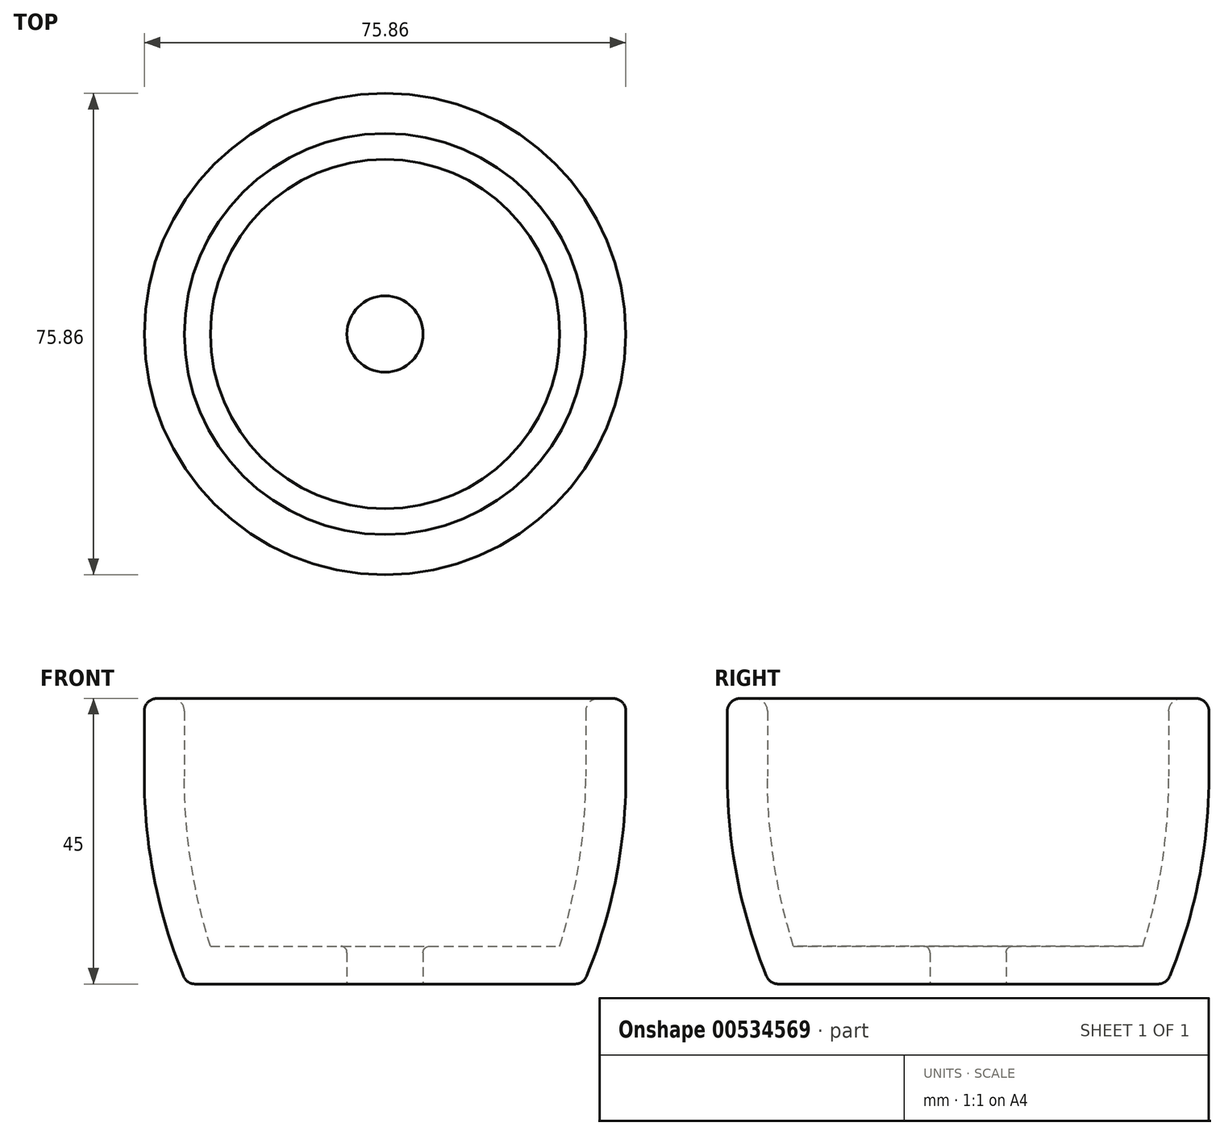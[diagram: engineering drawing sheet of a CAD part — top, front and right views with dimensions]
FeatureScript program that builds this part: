
annotation { "Feature Type Name" : "Feature", "Feature Type Description" : "" }
export const myFeature = defineFeature(function(context is Context, id is Id, definition is map)
    precondition{}
    {
        {
            var Q0;
            Q0=qCreatedBy(makeId("Front.planeOp"),FACE);
            var sketch = newSketch(context, id + "F0", { "sketchPlane" : qUnion([Q0])});
            skLineSegment(sketch, "E0", {"start": v(-37.93, 45) * mm, "end": v(-37.93, 32.73) * mm});
            skArc(sketch, "E1", {"start": v(-37.93, 32.73) * mm, "mid": v(-36.24, 16.03) * mm, "end": v(-31.24, 0) * mm});
            skLineSegment(sketch, "E2", {"start": v(-31.24, 0) * mm, "end": v(0, 0) * mm});
            skLineSegment(sketch, "E3", {"start": v(0, 0) * mm, "end": v(0, 5.95) * mm});
            skLineSegment(sketch, "E4", {"start": v(0, 5.95) * mm, "end": v(-27.52, 5.95) * mm});
            skLineSegment(sketch, "E5", {"start": v(-37.93, 45) * mm, "end": v(-31.61, 45) * mm});
            skLineSegment(sketch, "E6", {"start": v(-31.61, 45) * mm, "end": v(-31.61, 32.73) * mm});
            skArc(sketch, "E7", {"start": v(-31.61, 32.73) * mm, "mid": v(-30.58, 19.18) * mm, "end": v(-27.52, 5.95) * mm});
            skSolve(sketch);
        }
        {
            var Q0;
            Q0=makeQuery(id+"F0.imprint","IMPRINT",FACE,{"disambiguationData":[TD([[makeQuery(id+"F0.imprint","IMPRINT",EDGE,{"derivedFrom":sQuery(id+"F0.wireOp",EDGE,"E0")}),1.0]])]});
            var Q1;
            Q1=sQuery(id+"F0.wireOp",EDGE,"E3");
            revolve(context, id + "F1", {"entities" : qUnion([Q0]), "axis" : qUnion([Q1]), "revolveType" : RevolveType.FULL});
        }
        {
            var Q0;
            Q0=makeQuery(id+"F1.opRevolve","SWEPT_EDGE",EDGE,{"disambiguationData":[OSD([sQuery(id+"F0.wireOp",EDGE,"E5"),sQuery(id+"F0.wireOp",EDGE,"E6")])]});
            fillet(context, id + "F2", {"entities" : qUnion([Q0]), "radius" : 2 * mm, "tangentPropagation" : true, "allowEdgeOverflow" : false});
        }
        {
            var Q0;
            Q0=makeQuery(id+"F1.opRevolve","SWEPT_EDGE",EDGE,{"disambiguationData":[OSD([sQuery(id+"F0.wireOp",EDGE,"E0"),sQuery(id+"F0.wireOp",EDGE,"E5")])]});
            var Q1;
            Q1=makeQuery(id+"F1.opRevolve","SWEPT_EDGE",EDGE,{"disambiguationData":[OSD([sQuery(id+"F0.wireOp",EDGE,"E1"),sQuery(id+"F0.wireOp",EDGE,"E2")])]});
            fillet(context, id + "F3", {"entities" : qUnion([Q0, Q1]), "radius" : 2 * mm, "tangentPropagation" : true, "allowEdgeOverflow" : false});
        }
        {
            var Q0;
            Q0=makeQuery(id+"F1.opRevolve","SWEPT_FACE",FACE,{"disambiguationData":[OSD([sQuery(id+"F0.wireOp",EDGE,"E2")])]});
            var sketch = newSketch(context, id + "F4", { "sketchPlane" : qUnion([Q0])});
            skCircle(sketch, "E8", {"center": v(0, 0) * mm, "radius": 6 * mm});
            skSolve(sketch);
        }
        {
            var Q0;
            Q0=makeQuery(id+"F4.imprint","IMPRINT",FACE,{"disambiguationData":[TD([[makeQuery(id+"F4.imprint","IMPRINT",EDGE,{"derivedFrom":sQuery(id+"F4.wireOp",EDGE,"E8")}),1.0]])]});
            extrude(context, id + "F5", {"entities" : qUnion([Q0]), "operationType" : NewBodyOperationType.REMOVE, "oppositeDirection" : true, "depth" : 25 * mm, "offsetDistance" : 25 * mm});
        }
        {
            var Q0;
            Q0=makeQuery(id+"F5.boolean.opBoolean","COPY",EDGE,{"derivedFrom":makeQuery(id+"F5.opExtrude","CAP_EDGE",EDGE,{"disambiguationData":[OSD([sQuery(id+"F4.wireOp",EDGE,"E8")])],"isStart":true})});
            var Q1;
            Q1=makeQuery(id+"F5.boolean.opBoolean","INTERSECT",EDGE,{"derivedFrom":[makeQuery(id+"F1.opRevolve","SWEPT_FACE",FACE,{"disambiguationData":[OSD([sQuery(id+"F0.wireOp",EDGE,"E4")])]}),makeQuery(id+"F5.opExtrude","SWEPT_FACE",FACE,{"disambiguationData":[OSD([sQuery(id+"F4.wireOp",EDGE,"E8")])]})]});
            fillet(context, id + "F6", {"entities" : qUnion([Q0, Q1]), "radius" : 1 * mm, "tangentPropagation" : true, "allowEdgeOverflow" : false});
        }
    });
